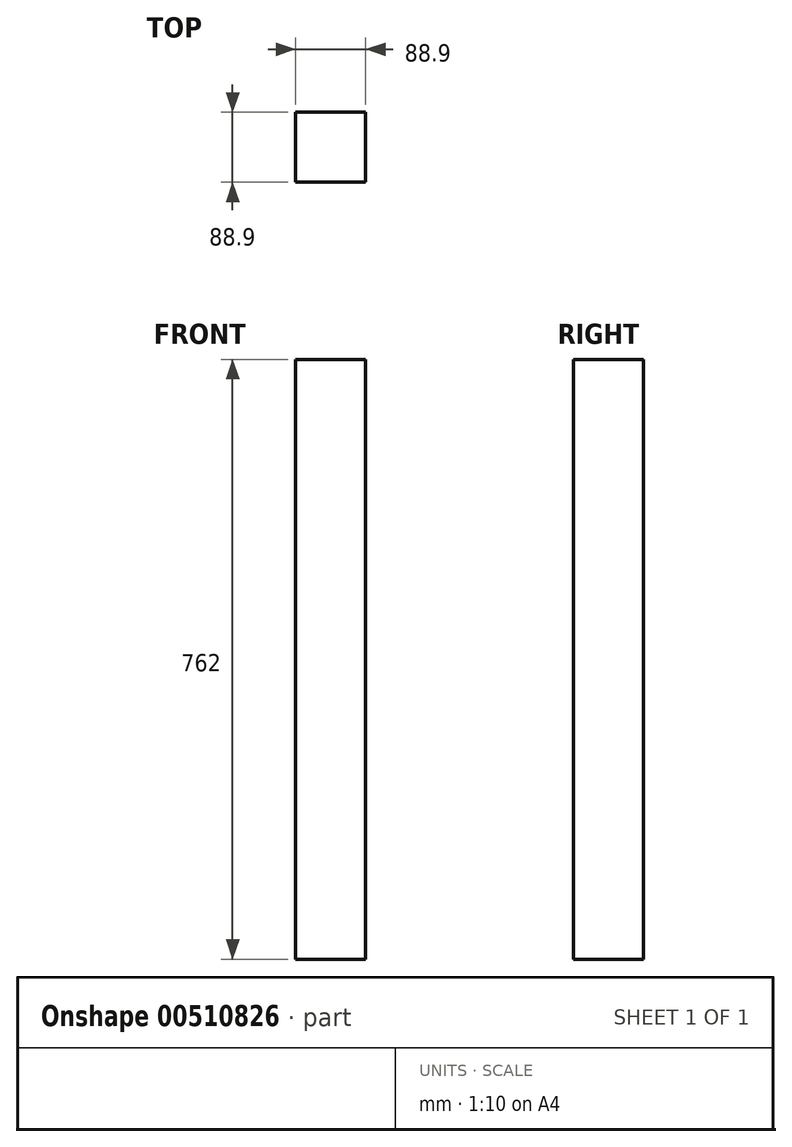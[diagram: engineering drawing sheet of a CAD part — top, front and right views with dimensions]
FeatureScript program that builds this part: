
annotation { "Feature Type Name" : "Feature", "Feature Type Description" : "" }
export const myFeature = defineFeature(function(context is Context, id is Id, definition is map)
    precondition{}
    {
        {
            var Q0;
            Q0=qCreatedBy(makeId("Top.planeOp"),FACE);
            var sketch = newSketch(context, id + "F0", { "sketchPlane" : qUnion([Q0])});
            skLineSegment(sketch, "E0", {"start": v(0, 44.45) * mm, "end": v(44.45, 44.45) * mm});
            skLineSegment(sketch, "E1", {"start": v(44.45, 44.45) * mm, "end": v(44.45, 0) * mm});
            skLineSegment(sketch, "E2.MirrorCS", {"start": v(-44.45, 44.45) * mm, "end": v(-44.45, 0) * mm});
            skLineSegment(sketch, "E3.MirrorCS", {"start": v(0, 44.45) * mm, "end": v(-44.45, 44.45) * mm});
            skLineSegment(sketch, "E4.MirrorCS", {"start": v(0, -44.45) * mm, "end": v(-44.45, -44.45) * mm});
            skLineSegment(sketch, "E5.MirrorCS", {"start": v(44.45, -44.45) * mm, "end": v(44.45, 0) * mm});
            skLineSegment(sketch, "E6.MirrorCS", {"start": v(0, -44.45) * mm, "end": v(44.45, -44.45) * mm});
            skLineSegment(sketch, "E7.MirrorCS", {"start": v(-44.45, -44.45) * mm, "end": v(-44.45, 0) * mm});
            skSolve(sketch);
        }
        {
            var Q0;
            Q0 = qSketchRegion(id + "F0", true);
            extrude(context, id + "F1", {"entities" : qUnion([Q0]), "depth" : 762 * mm});
        }
    });
